# Revit family: FU_Inspec_Campus_4-1
name_source: partatom
category: Furniture
units: mm (PartAtom-declared; Revit-internal decimal feet)

## family parameters
Always vertical = Yes
Cut with Voids When Loaded = No
OmniClass Number = 23.40.20.00
OmniClass Title = General Furniture and Specialties
Room Calculation Point = No
Shared = No
Work Plane-Based = No

## types (3) — shared parameters
Assembly Code = E2020
Description = *Please enter mtrl description here for use in mto*
Keynote = 46.B
Manufacturer = LAMMHULTS
Model = CAMPUS
URL = www.lammhults.se
zero-valued in all types: Default Elevation

## per-type parameters (varying)
| type | Back Material | Frame Material | Seat Material |
| Campus 4.1 - White - White | Laminate - Compact - White | Metal - White - Matte | Laminate - Compact - White |
| Campus 4.2 - Graphite - Blue - White | Laminate - Compact - White | Metal - Graphite - Matte | Fabric - Canvas - Blue |
| Campus 4.3 - Chrome - Blue | Fabric - Canvas - Blue | Metal - Chrome - Polished | Fabric - Canvas - Blue |

## geometry (parser evidence)
native form markers: Blend x20, Sweep x3
no freeform markers — native parametric forms only
